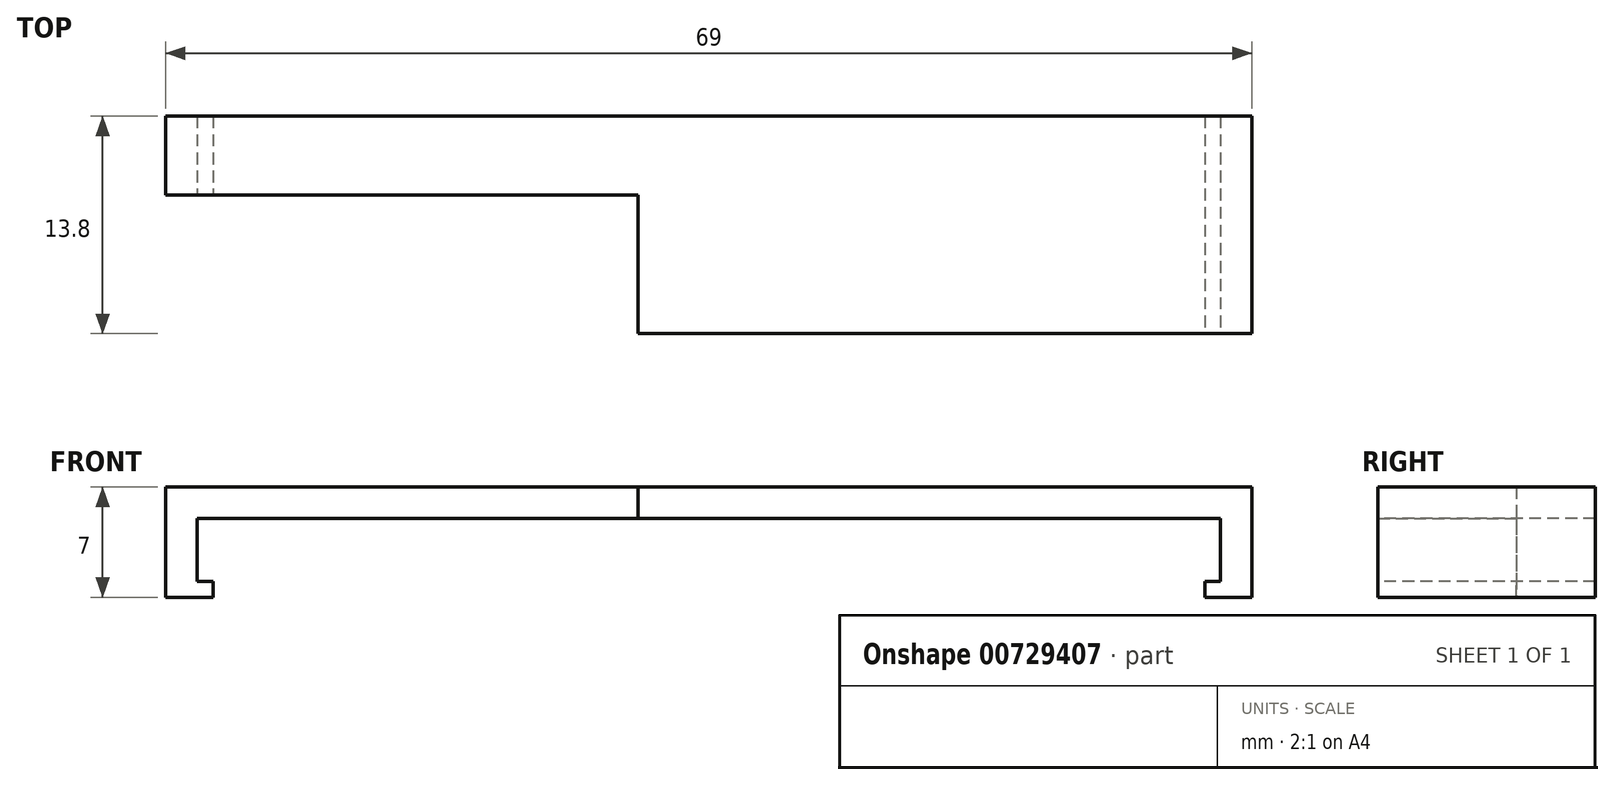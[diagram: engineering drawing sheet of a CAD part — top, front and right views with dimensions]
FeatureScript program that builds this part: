
annotation { "Feature Type Name" : "Feature", "Feature Type Description" : "" }
export const myFeature = defineFeature(function(context is Context, id is Id, definition is map)
    precondition{}
    {
        {
            var Q0;
            Q0=qCreatedBy(makeId("Top.planeOp"),FACE);
            var sketch = newSketch(context, id + "F0", { "sketchPlane" : qUnion([Q0])});
            skLineSegment(sketch, "E0.bottom", {"start": v(-32.29, 16.72) * mm, "end": v(36.71, 16.72) * mm});
            skLineSegment(sketch, "E0.top", {"start": v(-32.29, -17.1) * mm, "end": v(36.71, -17.1) * mm});
            skLineSegment(sketch, "E0.left", {"start": v(-32.29, 16.72) * mm, "end": v(-32.29, -17.1) * mm});
            skLineSegment(sketch, "E0.right", {"start": v(36.71, 16.72) * mm, "end": v(36.71, -17.1) * mm});
            skSolve(sketch);
        }
        {
            var Q0;
            Q0 = qSketchRegion(id + "F0", true);
            extrude(context, id + "F1", {"entities" : qUnion([Q0]), "depth" : 2 * mm, "offsetDistance" : 25 * mm});
        }
        {
            var Q0;
            Q0=makeQuery(id+"F1.opExtrude","CAP_FACE",FACE,{"disambiguationData":[OSD([sQuery(id+"F0.wireOp",EDGE,"E0.bottom"),sQuery(id+"F0.wireOp",EDGE,"E0.top"),sQuery(id+"F0.wireOp",EDGE,"E0.left"),sQuery(id+"F0.wireOp",EDGE,"E0.right")])],"isStart":true});
            var sketch = newSketch(context, id + "F2", { "sketchPlane" : qUnion([Q0])});
            skLineSegment(sketch, "E1.bottom", {"start": v(-32.29, 17.1) * mm, "end": v(-2.29, 17.1) * mm});
            skLineSegment(sketch, "E1.top", {"start": v(-32.29, 8.3) * mm, "end": v(-2.29, 8.3) * mm});
            skLineSegment(sketch, "E1.left", {"start": v(-32.29, 17.1) * mm, "end": v(-32.29, 8.3) * mm});
            skLineSegment(sketch, "E1.right", {"start": v(-2.29, 17.1) * mm, "end": v(-2.29, 8.3) * mm});
            skSolve(sketch);
        }
        {
            var Q0;
            Q0 = qSketchRegion(id + "F2", true);
            extrude(context, id + "F3", {"entities" : qUnion([Q0]), "operationType" : NewBodyOperationType.REMOVE, "oppositeDirection" : true, "depth" : 25 * mm, "offsetDistance" : 25 * mm});
        }
        {
            var Q0;
            Q0=makeQuery(id+"F1.opExtrude","CAP_FACE",FACE,{"disambiguationData":[OSD([sQuery(id+"F0.wireOp",EDGE,"E0.bottom"),sQuery(id+"F0.wireOp",EDGE,"E0.top"),sQuery(id+"F0.wireOp",EDGE,"E0.left"),sQuery(id+"F0.wireOp",EDGE,"E0.right")])],"isStart":false});
            var sketch = newSketch(context, id + "F4", { "sketchPlane" : qUnion([Q0])});
            skLineSegment(sketch, "E2.bottom", {"start": v(-32.29, 16.72) * mm, "end": v(36.71, 16.72) * mm});
            skLineSegment(sketch, "E2.top", {"start": v(-32.29, -3.3) * mm, "end": v(36.71, -3.3) * mm});
            skLineSegment(sketch, "E2.left", {"start": v(-32.29, 16.72) * mm, "end": v(-32.29, -3.3) * mm});
            skLineSegment(sketch, "E2.right", {"start": v(36.71, 16.72) * mm, "end": v(36.71, -3.3) * mm});
            skSolve(sketch);
        }
        {
            var Q0;
            Q0 = qSketchRegion(id + "F4", true);
            extrude(context, id + "F5", {"entities" : qUnion([Q0]), "operationType" : NewBodyOperationType.REMOVE, "oppositeDirection" : true, "depth" : 25 * mm, "offsetDistance" : 25 * mm});
        }
        {
            var Q0;
            Q0=makeQuery(id+"F1.opExtrude","CAP_FACE",FACE,{"disambiguationData":[OSD([sQuery(id+"F0.wireOp",EDGE,"E0.bottom"),sQuery(id+"F0.wireOp",EDGE,"E0.top"),sQuery(id+"F0.wireOp",EDGE,"E0.left"),sQuery(id+"F0.wireOp",EDGE,"E0.right")])],"isStart":true});
            var sketch = newSketch(context, id + "F6", { "sketchPlane" : qUnion([Q0])});
            skLineSegment(sketch, "E3.bottom", {"start": v(-32.29, 8.3) * mm, "end": v(-29.29, 8.3) * mm});
            skLineSegment(sketch, "E3.top", {"start": v(-32.29, 3.3) * mm, "end": v(-29.29, 3.3) * mm});
            skLineSegment(sketch, "E3.left", {"start": v(-32.29, 8.3) * mm, "end": v(-32.29, 3.3) * mm});
            skLineSegment(sketch, "E3.right", {"start": v(-29.29, 8.3) * mm, "end": v(-29.29, 3.3) * mm});
            skLineSegment(sketch, "E4.bottom", {"start": v(36.71, 17.1) * mm, "end": v(33.71, 17.1) * mm});
            skLineSegment(sketch, "E4.top", {"start": v(36.71, 3.3) * mm, "end": v(33.71, 3.3) * mm});
            skLineSegment(sketch, "E4.left", {"start": v(36.71, 17.1) * mm, "end": v(36.71, 3.3) * mm});
            skLineSegment(sketch, "E4.right", {"start": v(33.71, 17.1) * mm, "end": v(33.71, 3.3) * mm});
            skSolve(sketch);
        }
        {
            var Q0;
            Q0 = qSketchRegion(id + "F6", true);
            extrude(context, id + "F7", {"entities" : qUnion([Q0]), "operationType" : NewBodyOperationType.ADD, "depth" : 5 * mm, "offsetDistance" : 25 * mm});
        }
        {
            var Q0;
            Q0=makeQuery(id+"F7.boolean.opBoolean","MERGE",FACE,{"derivedFrom":[makeQuery(id+"F1.opExtrude","SWEPT_FACE",FACE,{"disambiguationData":[OSD([sQuery(id+"F0.wireOp",EDGE,"E0.top")])]}),makeQuery(id+"F7.opExtrude","SWEPT_FACE",FACE,{"disambiguationData":[OSD([sQuery(id+"F6.wireOp",EDGE,"E4.bottom")])]})]});
            var sketch = newSketch(context, id + "F8", { "sketchPlane" : qUnion([Q0])});
            skLineSegment(sketch, "E5", {"start": v(33.71, -5) * mm, "end": v(33.71, -4) * mm});
            skLineSegment(sketch, "E6", {"start": v(33.71, -4) * mm, "end": v(34.71, -4) * mm});
            skLineSegment(sketch, "E7", {"start": v(34.71, -4) * mm, "end": v(34.71, 0) * mm});
            skLineSegment(sketch, "E8", {"start": v(34.71, 0) * mm, "end": v(33.71, 0) * mm});
            skLineSegment(sketch, "E9", {"start": v(33.71, 0) * mm, "end": v(33.71, -4) * mm});
            skSolve(sketch);
        }
        {
            var Q0;
            Q0 = qSketchRegion(id + "F8", true);
            extrude(context, id + "F9", {"entities" : qUnion([Q0]), "operationType" : NewBodyOperationType.REMOVE, "oppositeDirection" : true, "depth" : 25 * mm, "offsetDistance" : 25 * mm});
        }
        {
            var Q0;
            Q0=makeQuery(id+"F7.boolean.opBoolean","MERGE",FACE,{"derivedFrom":[makeQuery(id+"F3.boolean.opBoolean","COPY",FACE,{"derivedFrom":makeQuery(id+"F3.opExtrude","SWEPT_FACE",FACE,{"disambiguationData":[OSD([sQuery(id+"F2.wireOp",EDGE,"E1.top")])]})}),makeQuery(id+"F7.opExtrude","SWEPT_FACE",FACE,{"disambiguationData":[OSD([sQuery(id+"F6.wireOp",EDGE,"E3.bottom")])]})]});
            var sketch = newSketch(context, id + "F10", { "sketchPlane" : qUnion([Q0])});
            skLineSegment(sketch, "E10.bottom", {"start": v(-29.29, 0) * mm, "end": v(-30.29, 0) * mm});
            skLineSegment(sketch, "E10.top", {"start": v(-29.29, -4) * mm, "end": v(-30.29, -4) * mm});
            skLineSegment(sketch, "E10.left", {"start": v(-29.29, 0) * mm, "end": v(-29.29, -4) * mm});
            skLineSegment(sketch, "E10.right", {"start": v(-30.29, 0) * mm, "end": v(-30.29, -4) * mm});
            skSolve(sketch);
        }
        {
            var Q0;
            Q0 = qSketchRegion(id + "F10", true);
            extrude(context, id + "F11", {"entities" : qUnion([Q0]), "operationType" : NewBodyOperationType.REMOVE, "oppositeDirection" : true, "depth" : 25 * mm, "offsetDistance" : 25 * mm});
        }
    });
